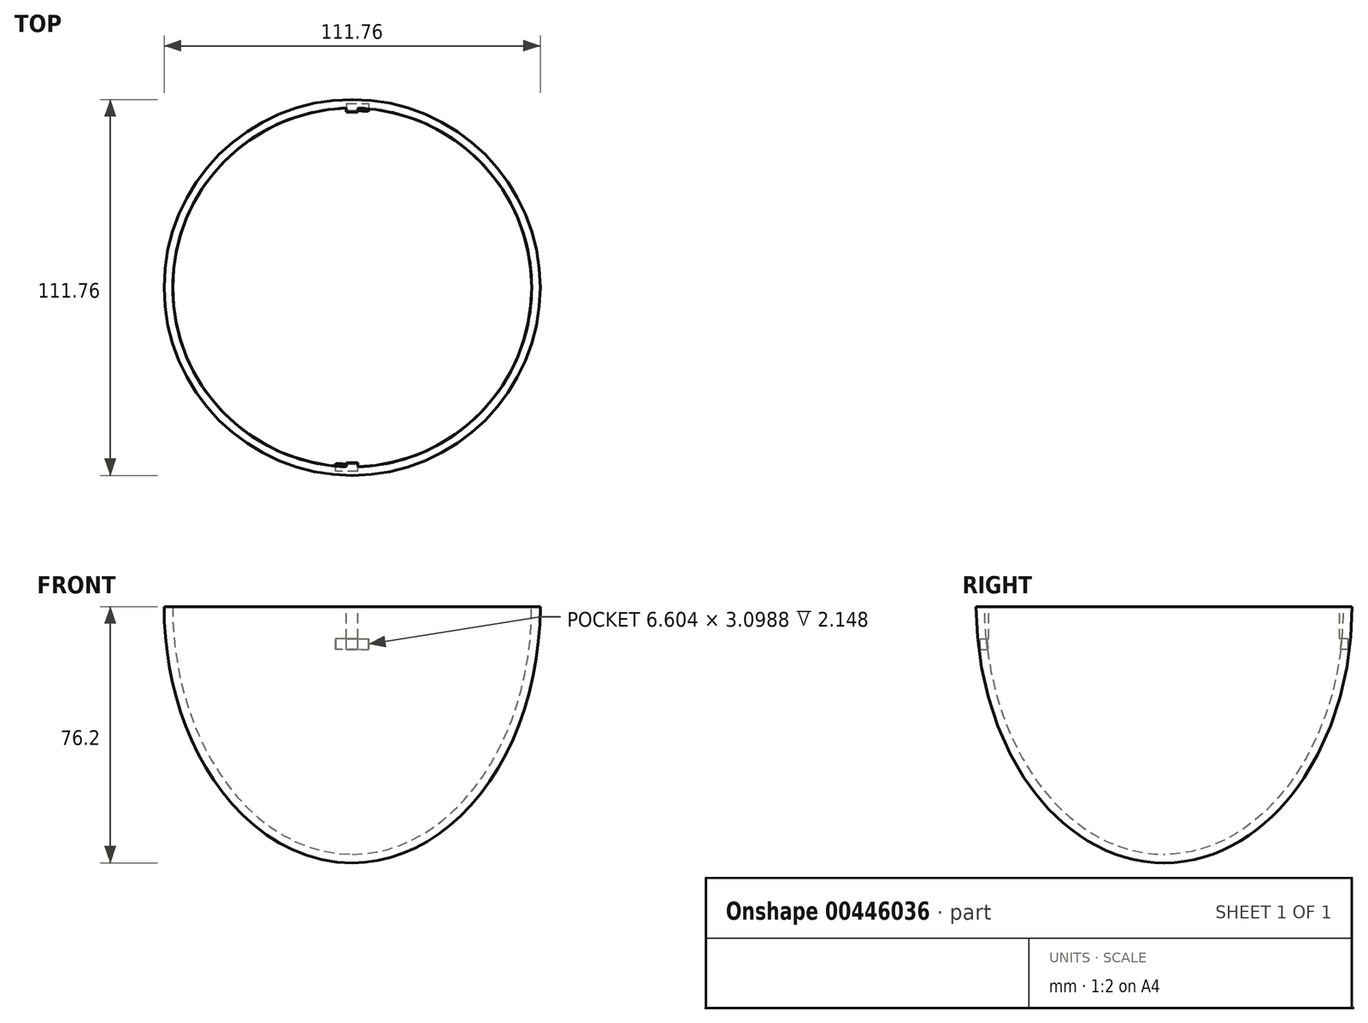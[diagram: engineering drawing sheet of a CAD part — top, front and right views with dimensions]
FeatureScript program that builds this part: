
annotation { "Feature Type Name" : "Feature", "Feature Type Description" : "" }
export const myFeature = defineFeature(function(context is Context, id is Id, definition is map)
    precondition{}
    {
        {
            var Q0;
            Q0=qCreatedBy(makeId("Front.planeOp"),FACE);
            var sketch = newSketch(context, id + "F0", { "sketchPlane" : qUnion([Q0])});
            skLineSegment(sketch, "E0", {"start": v(0, 113.49) * mm, "end": v(0, -38.91) * mm});
            skEllipse(sketch, "E1", {"center": v(0, 37.29) * mm, "majorRadius": 76.2 * mm, "minorRadius": 55.88 * mm, "majorAxis": v(0, 1)});
            skLineSegment(sketch, "E2", {"start": v(0, 37.29) * mm, "end": v(55.88, 37.29) * mm});
            skSolve(sketch);
        }
        {
            var Q0;
            {var subQ3=sQuery(id+"F0.wireOp",EDGE,"E2");Q0=makeQuery(id+"F0.imprint","IMPRINT",FACE,{"disambiguationData":[TD([[makeQuery(id+"F0.imprint","IMPRINT",EDGE,{"derivedFrom":subQ3}),-1.0]])]});}
            var Q1;
            Q1=sQuery(id+"F0.wireOp",EDGE,"E0");
            revolve(context, id + "F1", {"entities" : qUnion([Q0]), "axis" : qUnion([Q1]), "revolveType" : RevolveType.ONE_DIRECTION, "oppositeDirection" : true, "angle" : 360 * degree});
        }
        {
            var Q0;
            Q0=makeQuery(id+"F1.opRevolve","SWEPT_FACE",FACE,{"disambiguationData":[OSD([sQuery(id+"F0.wireOp",EDGE,"E2")])]});
            shell(context, id + "F2", {"entities" : qUnion([Q0]), "thickness" : 2.54 * mm});
        }
        {
            var Q0;
            Q0=makeQuery(id+"F1.opRevolve","SWEPT_FACE",FACE,{"disambiguationData":[OSD([sQuery(id+"F0.wireOp",EDGE,"E2")])]});
            var sketch = newSketch(context, id + "F3", { "sketchPlane" : qUnion([Q0])});
            skLineSegment(sketch, "E3.MirrorCS", {"start": v(0, 53.23) * mm, "end": v(-1.68, 53.23) * mm});
            skLineSegment(sketch, "E4", {"start": v(-1.68, 54.66) * mm, "end": v(-1.68, 53.23) * mm});
            skLineSegment(sketch, "E5", {"start": v(0, 53.23) * mm, "end": v(0, 54.66) * mm});
            skLineSegment(sketch, "E6", {"start": v(0, 54.66) * mm, "end": v(-1.68, 54.66) * mm});
            skLineSegment(sketch, "E7.MirrorCS", {"start": v(0, 54.66) * mm, "end": v(1.68, 54.66) * mm});
            skLineSegment(sketch, "E8.MirrorCS", {"start": v(1.68, 54.66) * mm, "end": v(1.68, 53.23) * mm});
            skLineSegment(sketch, "E9.MirrorCS", {"start": v(0, 53.23) * mm, "end": v(1.68, 53.23) * mm});
            skLineSegment(sketch, "E10", {"start": v(-53.34, 0) * mm, "end": v(53.34, 0) * mm});
            skLineSegment(sketch, "E11.MirrorCS", {"start": v(1.68, -54.66) * mm, "end": v(1.68, -53.23) * mm});
            skLineSegment(sketch, "E12.MirrorCS", {"start": v(0, -54.66) * mm, "end": v(1.68, -54.66) * mm});
            skLineSegment(sketch, "E13.MirrorCS", {"start": v(0, -54.66) * mm, "end": v(-1.68, -54.66) * mm});
            skLineSegment(sketch, "E14.MirrorCS", {"start": v(-1.68, -54.66) * mm, "end": v(-1.68, -53.23) * mm});
            skLineSegment(sketch, "E15.MirrorCS", {"start": v(0, -53.23) * mm, "end": v(-1.68, -53.23) * mm});
            skLineSegment(sketch, "E16.MirrorCS", {"start": v(0, -53.23) * mm, "end": v(1.68, -53.23) * mm});
            skSolve(sketch);
        }
        {
            var Q0;
            {var subQ0=sQuery(id+"F3.wireOp",EDGE,"r1mQ6fz2-V4OR-sCXk-bxVT-CCtKPG448bru");Q0=makeQuery(id+"F3.imprint","IMPRINT",FACE,{"disambiguationData":[TD([[makeQuery(id+"F3.imprint","IMPRINT",EDGE,{"derivedFrom":subQ0}),1.0]])]});}
            var Q1;
            {var subQ0=sQuery(id+"F3.wireOp",EDGE,"E6");Q1=makeQuery(id+"F3.imprint","IMPRINT",FACE,{"disambiguationData":[TD([[makeQuery(id+"F3.imprint","IMPRINT",EDGE,{"derivedFrom":subQ0}),1.0]])]});}
            var Q2;
            {var subQ0=sQuery(id+"F3.wireOp",EDGE,"E7.MirrorCS");Q2=makeQuery(id+"F3.imprint","IMPRINT",FACE,{"disambiguationData":[TD([[makeQuery(id+"F3.imprint","IMPRINT",EDGE,{"derivedFrom":subQ0}),-1.0]])]});}
            var Q3;
            {var subQ0=sQuery(id+"F3.wireOp",EDGE,"E3.MirrorCS");Q3=makeQuery(id+"F3.imprint","IMPRINT",FACE,{"disambiguationData":[TD([[makeQuery(id+"F3.imprint","IMPRINT",EDGE,{"derivedFrom":subQ0}),-1.0]])]});}
            var Q4;
            {var subQ0=sQuery(id+"F3.wireOp",EDGE,"E9.MirrorCS");Q4=makeQuery(id+"F3.imprint","IMPRINT",FACE,{"disambiguationData":[TD([[makeQuery(id+"F3.imprint","IMPRINT",EDGE,{"derivedFrom":subQ0}),1.0]])]});}
            var Q5;
            {var subQ6=sQuery(id+"F3.wireOp",EDGE,"E12.MirrorCS");Q5=makeQuery(id+"F3.imprint","IMPRINT",FACE,{"disambiguationData":[TD([[makeQuery(id+"F3.imprint","IMPRINT",EDGE,{"derivedFrom":subQ6}),1.0]])]});}
            extrude(context, id + "F4", {"entities" : qUnion([Q0, Q1, Q2, Q3, Q4, Q5]), "operationType" : NewBodyOperationType.REMOVE, "oppositeDirection" : true, "depth" : 12.7 * mm});
        }
        {
            var Q0;
            Q0=makeQuery(id+"F4.boolean.opBoolean","COPY",FACE,{"derivedFrom":makeQuery(id+"F4.opExtrude","SWEPT_FACE",FACE,{"disambiguationData":[OSD([sQuery(id+"F3.wireOp",EDGE,"E6"),sQuery(id+"F3.wireOp",EDGE,"E7.MirrorCS")])]})});
            extrude(context, id + "F5", {"entities" : qUnion([Q0]), "operationType" : NewBodyOperationType.ADD, "depth" : 2.54 * mm});
        }
        {
            var Q0;
            Q0=makeQuery(id+"F5.opExtrude","CAP_FACE",FACE,{"disambiguationData":[OSD([sQuery(id+"F3.wireOp",EDGE,"E6"),sQuery(id+"F3.wireOp",EDGE,"E7.MirrorCS")])],"isStart":false});
            var sketch = newSketch(context, id + "F6", { "sketchPlane" : qUnion([Q0])});
            skLineSegment(sketch, "E17.bottom", {"start": v(-1.68, 24.59) * mm, "end": v(4.92, 24.59) * mm});
            skLineSegment(sketch, "E17.top", {"start": v(-1.68, 27.69) * mm, "end": v(4.92, 27.69) * mm});
            skLineSegment(sketch, "E17.left", {"start": v(-1.68, 24.59) * mm, "end": v(-1.68, 27.69) * mm});
            skLineSegment(sketch, "E17.right", {"start": v(4.92, 24.59) * mm, "end": v(4.92, 27.69) * mm});
            skSolve(sketch);
        }
        {
            var Q0;
            {var subQ3=sQuery(id+"F6.wireOp",EDGE,"E17.right");Q0=makeQuery(id+"F6.imprint","IMPRINT",FACE,{"disambiguationData":[TD([[makeQuery(id+"F6.imprint","IMPRINT",EDGE,{"derivedFrom":subQ3}),1.0]])]});}
            var Q1;
            {var subQ0=sQuery(id+"F6.wireOp",EDGE,"E17.left");Q1=makeQuery(id+"F6.imprint","IMPRINT",FACE,{"disambiguationData":[TD([[makeQuery(id+"F6.imprint","IMPRINT",EDGE,{"derivedFrom":subQ0}),-1.0]])]});}
            var Q2;
            {var subQ1=sQuery(id+"F3.wireOp",EDGE,"E6");var subQ4=sQuery(id+"F3.wireOp",EDGE,"E7.MirrorCS");var subQ7=makeQuery(id+"F5.opExtrude","CAP_EDGE",EDGE,{"disambiguationData":[OSD([subQ1,subQ4]),TDD([makeQuery(id+"F4.boolean.opBoolean","COPY",EDGE,{"derivedFrom":makeQuery(id+"F4.opExtrude","CAP_EDGE",EDGE,{"disambiguationData":[OSD([subQ1,subQ4])],"isStart":true})})])],"isStart":false});Q2=makeQuery(id+"F6.imprint","IMPRINT",FACE,{"disambiguationData":[TD([[makeQuery(id+"F6.imprint","IMPRINT",EDGE,{"derivedFrom":subQ7}),1.0]])]});}
            extrude(context, id + "F7", {"entities" : qUnion([Q0, Q1, Q2]), "operationType" : NewBodyOperationType.REMOVE, "oppositeDirection" : true, "depth" : 2.54 * mm});
        }
        {
            var Q0;
            Q0=makeQuery(id+"F4.boolean.opBoolean","COPY",FACE,{"derivedFrom":makeQuery(id+"F4.opExtrude","SWEPT_FACE",FACE,{"disambiguationData":[OSD([sQuery(id+"F3.wireOp",EDGE,"E12.MirrorCS"),sQuery(id+"F3.wireOp",EDGE,"E13.MirrorCS")])]})});
            extrude(context, id + "F8", {"entities" : qUnion([Q0]), "operationType" : NewBodyOperationType.ADD, "depth" : 2.54 * mm});
        }
        {
            var Q0;
            Q0=makeQuery(id+"F8.opExtrude","CAP_FACE",FACE,{"disambiguationData":[OSD([sQuery(id+"F3.wireOp",EDGE,"E12.MirrorCS"),sQuery(id+"F3.wireOp",EDGE,"E13.MirrorCS")])],"isStart":false});
            var sketch = newSketch(context, id + "F9", { "sketchPlane" : qUnion([Q0])});
            skLineSegment(sketch, "E18.bottom", {"start": v(-1.68, 24.59) * mm, "end": v(4.92, 24.59) * mm});
            skLineSegment(sketch, "E18.top", {"start": v(-1.68, 27.69) * mm, "end": v(4.92, 27.69) * mm});
            skLineSegment(sketch, "E18.left", {"start": v(-1.68, 24.59) * mm, "end": v(-1.68, 27.69) * mm});
            skLineSegment(sketch, "E18.right", {"start": v(4.92, 24.59) * mm, "end": v(4.92, 27.69) * mm});
            skSolve(sketch);
        }
        {
            var Q0;
            {var subQ3=sQuery(id+"F9.wireOp",EDGE,"E18.right");Q0=makeQuery(id+"F9.imprint","IMPRINT",FACE,{"disambiguationData":[TD([[makeQuery(id+"F9.imprint","IMPRINT",EDGE,{"derivedFrom":subQ3}),1.0]])]});}
            var Q1;
            {var subQ0=sQuery(id+"F9.wireOp",EDGE,"E18.left");Q1=makeQuery(id+"F9.imprint","IMPRINT",FACE,{"disambiguationData":[TD([[makeQuery(id+"F9.imprint","IMPRINT",EDGE,{"derivedFrom":subQ0}),-1.0]])]});}
            var Q2;
            {var subQ1=sQuery(id+"F3.wireOp",EDGE,"E12.MirrorCS");var subQ4=sQuery(id+"F3.wireOp",EDGE,"E13.MirrorCS");var subQ7=makeQuery(id+"F8.opExtrude","CAP_EDGE",EDGE,{"disambiguationData":[OSD([subQ1,subQ4]),TDD([makeQuery(id+"F4.boolean.opBoolean","COPY",EDGE,{"derivedFrom":makeQuery(id+"F4.opExtrude","CAP_EDGE",EDGE,{"disambiguationData":[OSD([subQ1,subQ4])],"isStart":true})})])],"isStart":false});Q2=makeQuery(id+"F9.imprint","IMPRINT",FACE,{"disambiguationData":[TD([[makeQuery(id+"F9.imprint","IMPRINT",EDGE,{"derivedFrom":subQ7}),-1.0]])]});}
            extrude(context, id + "F10", {"entities" : qUnion([Q0, Q1, Q2]), "operationType" : NewBodyOperationType.REMOVE, "oppositeDirection" : true, "depth" : 2.54 * mm});
        }
    });
